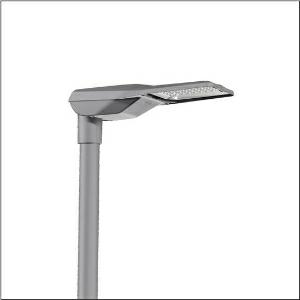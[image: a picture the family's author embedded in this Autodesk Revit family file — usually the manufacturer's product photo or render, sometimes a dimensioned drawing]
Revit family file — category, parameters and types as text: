
# Revit family: streetlight_sl_21_mini___st0_5a_5xe6b33a08gb_6f89
name_source: partatom
category: Lighting Fixtures
units: mm (PartAtom-declared; Revit-internal decimal feet)

## family parameters
Cut with Voids When Loaded = No
Host = Face
Light Source = No
Part Type = Normal
Room Calculation Point = No
Round Connector Dimension = Use Diameter
Shared = No

## types (1)
- --- (1 x LED, 5940 lm, 40.4 W, 3000K)
    Apparent Load = 40 VA
    CIE Flux Codes = 41 75 97 100 100
    Color Rendering = 70
    Color Temperature = 3000K
    Default Elevation = 1800 mm
    Description = Streetlight SL 21 mini, mast luminaire, primary light control with lens, of PMMA, primary optical cover: cover, of toughened safety glass, transparent, light distribution: ST0.5a, light emission: direct distribution, primary light characteristic: asymmetric, installation type: post-top, side-entry, LED, 3G 1.5mm², High Power LED, rated luminous flux: 5.940lm, luminous efficacy: 147lm/W, light colour: 730, colour temperature: 3000K, control gear: Easy, control: overheat protection, constant luminous flux control, time-dependent luminous flux control, flexible luminous flux parameterisation, mains connection: 230..240V, AC, 50/60Hz, connection cable pre-assembled, cable length: 6,5m, wiring characteristics: H07RN-F, start of lifetime: 40W, end of service life: 41W, reduction: 19W, luminaire housing, of diecast aluminium, powder-coated, Siteco® metallic grey (DB 702S), corrosivity category C5 mid according to DIN EN ISO 12944, please order mast flange separately, inclination adjustable: 0°, 5°, 10°, 15°, sealing non-destructively replaceable, multi-level sealing system, length: 628mm, width: 235mm, height: 110mm, mast flange for spigot size: 42mm (side-entry): 5XC10008XM4, 60/48mm (side-entry/post-top): 5XC10108XM2, 76/60mm (side-entry/post-top): 5XC10108XM1, mounting height: 4..8m, protection rating (complete): IP66, insulation class (complete): insulation class II (safety insulation), certification: CE, ENEC, ENEC+, VDE, impact resistance: IK10, permissible operating ambient temperature for outdoor applications: -40..+50°C, standard-compliant lighting for roads and squares, packaging unit: 1 piece

Light Distribution: ST0.5a
    Height = 110 mm
    Lamp = 1 x LED
    Lamp Light Flux = 5940 lm
    Lamp Power = 40.4 W
    Lamp count = 1
    Length = 625 mm
    Luminous efficacy = 147 lm/W
    Manufacturer = Siteco
    ModVariant = No
    Model = 5XE6B33A08GB
    Number of Poles = 1
    OnlyDefault = Yes
    Power Factor = 1
    Product Name = Streetlight SL 21 mini | ST0.5a
    Product group = mast luminaire | pylon top
    ProductGroupID = 6100
    Protection Class = Protection class II
    Protection Degree = IP 66
    RLX_Detail_Level = 1
    RLX_Emergency_Light_Flux = 0 lm
    RLX_Emergency_Type = 0
    RLX_Emergency_Type_DB = No
    RlxData = <blob elided: 37017 chars, md5=f4fb13f9>
    Socket = socket
    Standby Power = 0 W
    System Light Flux = 5940 lm
    System Power = 40 W
    Type Comments = factory setting: luminous flux: 100 % | Output Level: 100 % | 812 mA
    Type Image = l_1003519.jpg
    URL = http://relux.com
    VarID = @adj_212267
    Voltage = 0 V
    Weight = 0.00 kg
    Width = 234 mm

## geometry (parser evidence)
native form markers: Blend x4, Sweep x9
no freeform markers — native parametric forms only
